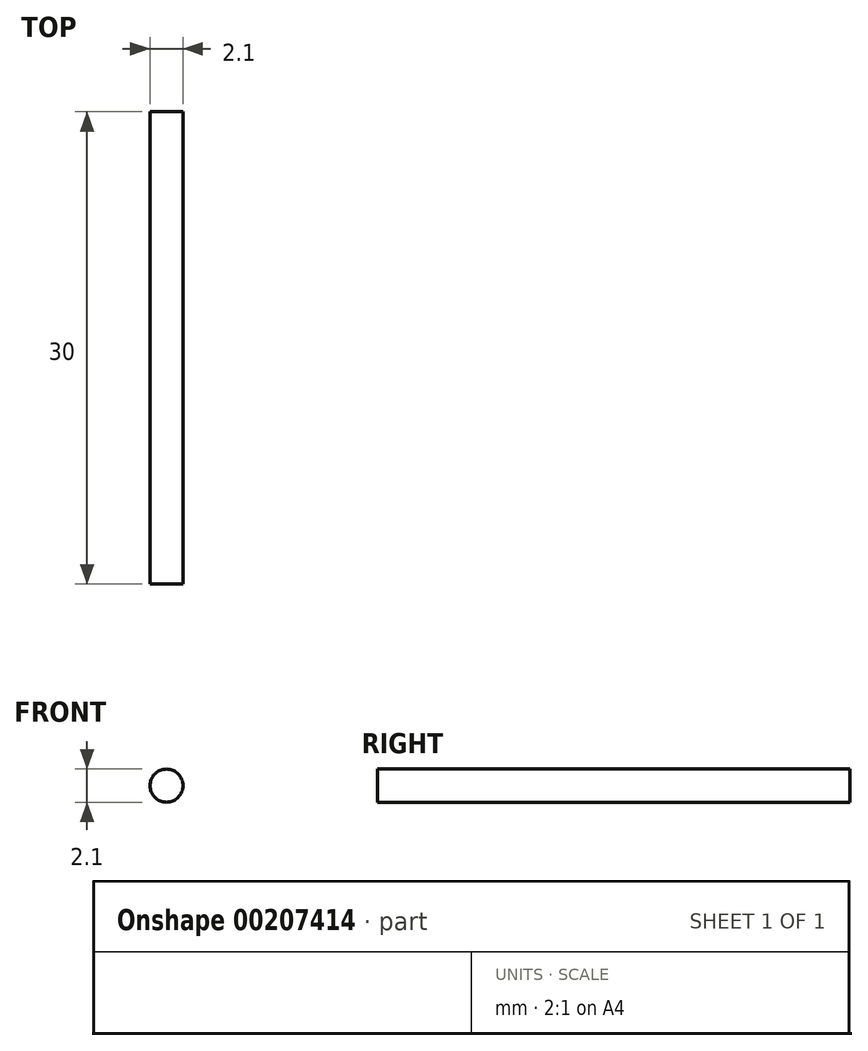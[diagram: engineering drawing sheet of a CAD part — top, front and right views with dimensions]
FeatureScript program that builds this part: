
annotation { "Feature Type Name" : "Feature", "Feature Type Description" : "" }
export const myFeature = defineFeature(function(context is Context, id is Id, definition is map)
    precondition{}
    {
        {
            var Q0;
            Q0=qCreatedBy(makeId("Front.planeOp"),FACE);
            var sketch = newSketch(context, id + "F0", { "sketchPlane" : qUnion([Q0])});
            skCircle(sketch, "E0", {"center": v(-110.14, 31.84) * mm, "radius": 1.05 * mm});
            skSolve(sketch);
        }
        {
            var Q0;
            Q0 = qSketchRegion(id + "F0", true);
            extrude(context, id + "F1", {"entities" : qUnion([Q0]), "depth" : 30 * mm});
        }
    });
